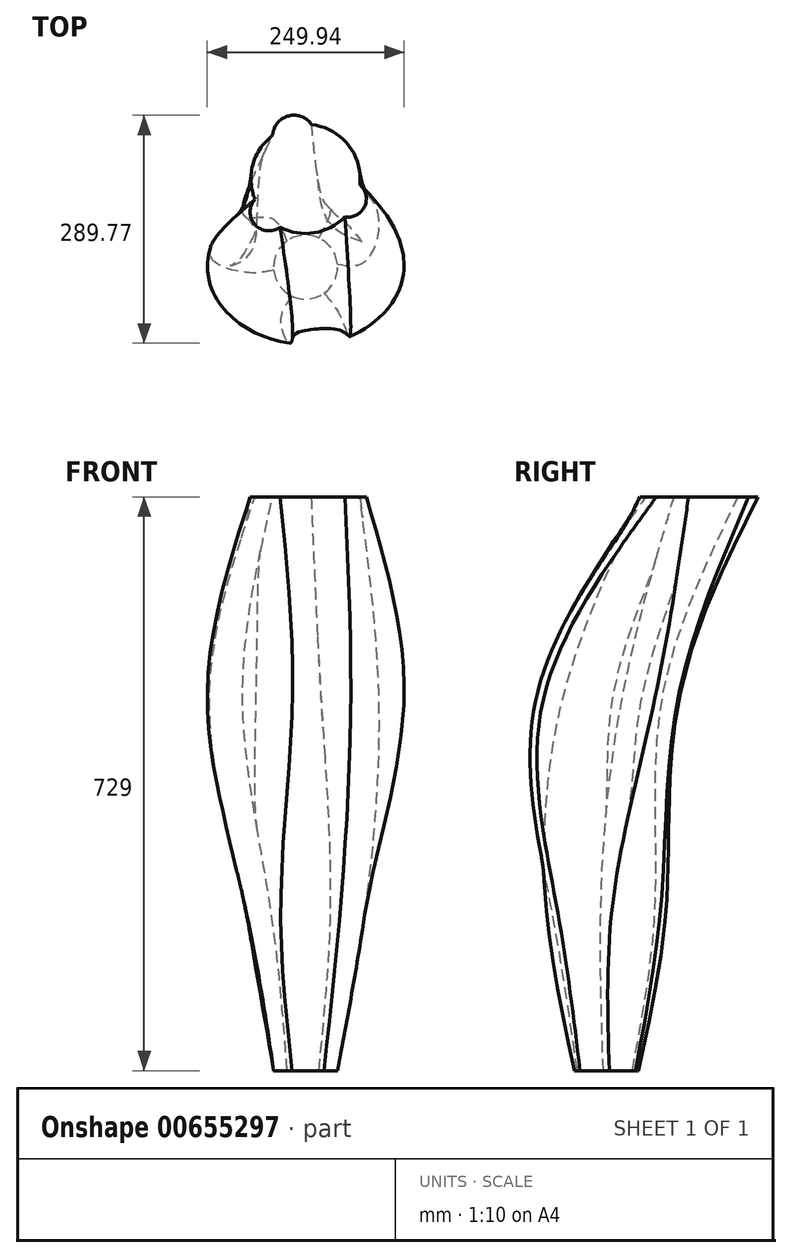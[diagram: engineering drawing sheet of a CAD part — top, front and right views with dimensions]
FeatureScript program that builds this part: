
annotation { "Feature Type Name" : "Feature", "Feature Type Description" : "" }
export const myFeature = defineFeature(function(context is Context, id is Id, definition is map)
    precondition{}
    {
        {
            var Q0;
            Q0=qCreatedBy(makeId("Top.planeOp"),FACE);
            var sketch = newSketch(context, id + "F0", { "sketchPlane" : qUnion([Q0])});
            skCircle(sketch, "E0", {"center": v(0, 0) * mm, "radius": 40.62 * mm});
            skPoint(sketch, "E1", {"position": v(21.03, -34.75) * mm});
            skSolve(sketch);
        }
        {
            var Q0;
            Q0=qCreatedBy(makeId("Top.planeOp"),FACE);
            cPlane(context, id + "F1", {"entities" : qUnion([Q0]), "cplaneType" : CPlaneType.OFFSET, "offset" : 202 * mm, "width" : 150 * mm, "height" : 150 * mm});
        }
        {
            var Q0;
            Q0=qCreatedBy(id+"F1.planeOp",FACE);
            var sketch = newSketch(context, id + "F2", { "sketchPlane" : qUnion([Q0])});
            skCircle(sketch, "E2", {"center": v(0, 0) * mm, "radius": 75.75 * mm});
            skPoint(sketch, "E3", {"position": v(52.46, -54.64) * mm});
            skSolve(sketch);
        }
        {
            var Q0;
            Q0=qCreatedBy(id+"F1.planeOp",FACE);
            cPlane(context, id + "F3", {"entities" : qUnion([Q0]), "cplaneType" : CPlaneType.OFFSET, "offset" : 265 * mm, "width" : 150 * mm, "height" : 150 * mm});
        }
        {
            var Q0;
            Q0=qCreatedBy(id+"F3.planeOp",FACE);
            var sketch = newSketch(context, id + "F4", { "sketchPlane" : qUnion([Q0])});
            skEllipticalArc(sketch, "E4", {});
            skArc(sketch, "E5", {"start": v(57.31, -81.04) * mm, "mid": v(16.64, -56.9) * mm, "end": v(-16.74, -90.4) * mm});
            skArc(sketch, "E6", {"start": v(20.64, 89.98) * mm, "mid": v(45.57, 46.99) * mm, "end": v(93.39, 60.52) * mm});
            skArc(sketch, "E7", {"start": v(-122, 19.2) * mm, "mid": v(-70.6, 19.53) * mm, "end": v(-79.87, 70.1) * mm});
            skEllipticalArc(sketch, "E8.trimOffspring", {});
            skEllipticalArc(sketch, "E9.trimOffspring", {});
            const initialGuessF4  = {"E4": [0, 0, 1, 0, 0.12480074167251587, 0.09123212772657083, 5.189536705325853, 0.7252836873303927], "E8.trimOffspring": [0, 0, 1, 0, 0.12480074167251587, 0.09123212772657083, 1.404679049118914, 2.2652709556146204], "E9.trimOffspring": [0, 0, 1, 0, 0.12480074167251587, 0.09123212772657083, 2.9296352837728707, 4.577849302979147]};
            skSetInitialGuess(sketch, initialGuessF4);
            skSolve(sketch);
        }
        {
            var Q0;
            Q0=qCreatedBy(makeId("Top.planeOp"),FACE);
            cPlane(context, id + "F5", {"entities" : qUnion([Q0]), "cplaneType" : CPlaneType.OFFSET, "offset" : 729 * mm, "width" : 150 * mm, "height" : 150 * mm});
        }
        {
            var Q0;
            Q0=qCreatedBy(id+"F5.planeOp",FACE);
            var sketch = newSketch(context, id + "F6", { "sketchPlane" : qUnion([Q0])});
            skArc(sketch, "E10", {"start": v(-32.37, 50.69) * mm, "mid": v(10.95, 43.54) * mm, "end": v(49.88, 63.84) * mm});
            skPoint(sketch, "E11", {"position": v(0, 42.67) * mm});
            skArc(sketch, "E12", {"start": v(-64.32, 86.1) * mm, "mid": v(-64.36, 53.95) * mm, "end": v(-32.37, 50.69) * mm});
            skArc(sketch, "E13", {"start": v(49.88, 63.84) * mm, "mid": v(74.94, 76.92) * mm, "end": v(68.93, 104.53) * mm});
            skArc(sketch, "E14", {"start": v(7.68, 180.9) * mm, "mid": v(-21.96, 191.95) * mm, "end": v(-41.8, 167.31) * mm});
            skArc(sketch, "E15.trimOffspring", {"start": v(68.93, 104.53) * mm, "mid": v(54.09, 155.38) * mm, "end": v(7.68, 180.9) * mm});
            skArc(sketch, "E16.trimOffspring", {"start": v(-41.8, 167.31) * mm, "mid": v(-66.81, 130.52) * mm, "end": v(-64.32, 86.1) * mm});
            skSolve(sketch);
        }
        {
            var Q0;
            Q0 = qSketchRegion(id + "F0", true);
            var Q1;
            Q1 = qSketchRegion(id + "F2", true);
            var Q2;
            Q2 = qSketchRegion(id + "F4", true);
            var Q3;
            Q3 = qSketchRegion(id + "F6", true);
            var Q4;
            Q4=sQuery(id+"F0.wireOp",VERTEX,"E1");
            var Q5;
            Q5=sQuery(id+"F2.wireOp",VERTEX,"E3");
            var Q6;
            Q6=sQuery(id+"F6.wireOp",VERTEX,"E11");
            loft(context, id + "F7", {"sheetProfilesArray" : [{ "sheetProfileEntities" : qUnion([Q0]) }, { "sheetProfileEntities" : qUnion([Q1]) }, { "sheetProfileEntities" : qUnion([Q2]) }, { "sheetProfileEntities" : qUnion([Q3]) }], "connections" : [{ "connectionEntities" : qUnion([Q4, Q5, Q6]), "connectionEdgeQueries" : qUnion([]), "connectionEdgeParameters" : [] }]});
        }
    });
